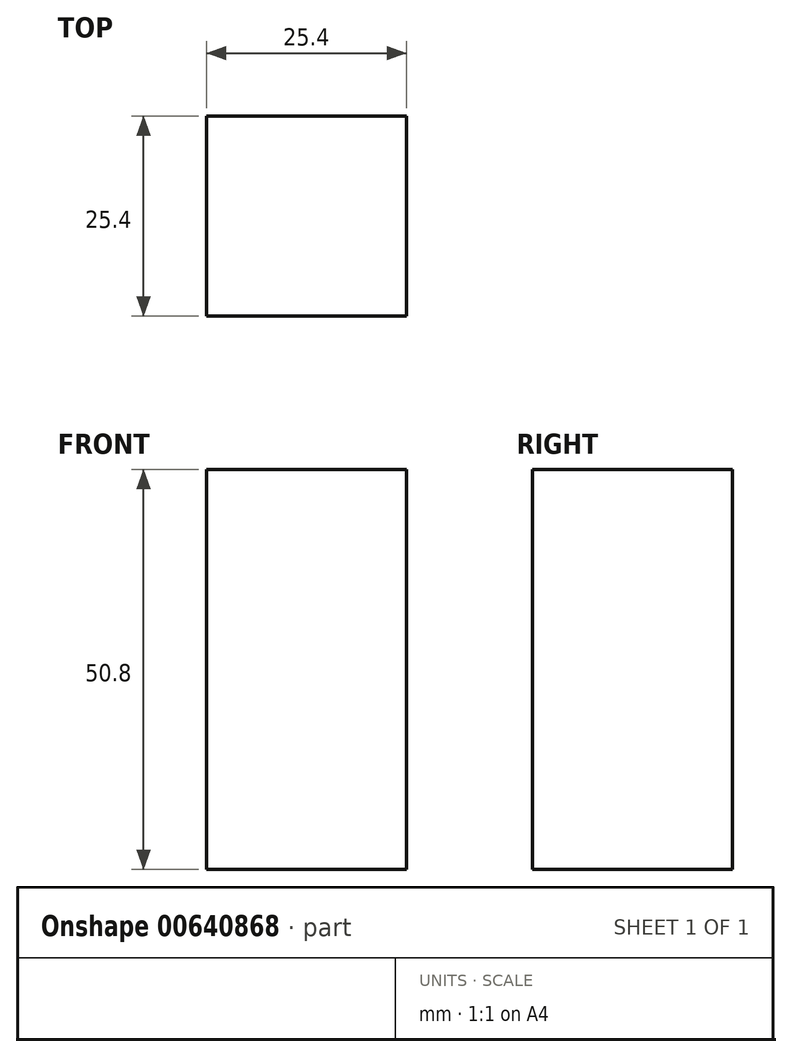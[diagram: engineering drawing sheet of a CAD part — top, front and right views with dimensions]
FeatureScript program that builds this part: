
annotation { "Feature Type Name" : "Feature", "Feature Type Description" : "" }
export const myFeature = defineFeature(function(context is Context, id is Id, definition is map)
    precondition{}
    {
        {
            var Q0;
            Q0=qCreatedBy(makeId("Top.planeOp"),FACE);
            var sketch = newSketch(context, id + "F0", { "sketchPlane" : qUnion([Q0])});
            skLineSegment(sketch, "E0.bottom", {"start": v(12.7, 12.7) * mm, "end": v(-12.7, 12.7) * mm});
            skLineSegment(sketch, "E0.top", {"start": v(12.7, -12.7) * mm, "end": v(-12.7, -12.7) * mm});
            skLineSegment(sketch, "E0.left", {"start": v(12.7, 12.7) * mm, "end": v(12.7, -12.7) * mm});
            skLineSegment(sketch, "E0.right", {"start": v(-12.7, 12.7) * mm, "end": v(-12.7, -12.7) * mm});
            skPoint(sketch, "E0.middle", {"position": v(0, 0) * mm});
            skSolve(sketch);
        }
        {
            var Q0;
            Q0=makeQuery(id+"F0.imprint","IMPRINT",FACE,{"disambiguationData":[TD([[makeQuery(id+"F0.imprint","IMPRINT",EDGE,{"derivedFrom":sQuery(id+"F0.wireOp",EDGE,"E0.bottom")}),1.0]])]});
            extrude(context, id + "F1", {"entities" : qUnion([Q0]), "depth" : 50.8 * mm, "offsetDistance" : 25.4 * mm});
        }
    });
